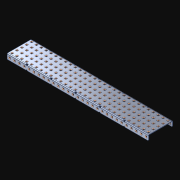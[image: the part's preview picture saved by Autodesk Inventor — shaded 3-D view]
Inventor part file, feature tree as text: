
AUTODESK INVENTOR PART (.ipt)
format: ipt  version: 2021 (Build 250183000, 183)  size: 2,302,976 bytes
history: native  units: in
note: dims shown in document units (in); Inventor stores cm internally (conversion verified against a paired STEP export)
features: extrude x204, other x204, sketch x4, pattern_linear x3
ambient origin geometry x8: Origin, YZ Plane, XZ Plane, XY Plane, X Axis, Y Axis, Z Axis, Center Point
bodies: Solid1 (feature_tree)
feature tree (415):
  pattern_linear  "Rectangular Pattern1"  Spacing1=0.182in  [1 undecoded]
  pattern_linear  "Rectangular Pattern2"  Spacing1=0.046in  [1 undecoded]
  pattern_linear  "Rectangular Pattern3"  Spacing1=0.5in  [1 undecoded]
  extrude  "Extrusion1"  Depth=0.046in
  sketch  "Sketch1"  dims[d0=0.182in]
  other  "Srf1"
  sketch  "Sketch2"  dims[d1=0.046in d2=0.0in]
  other  "Srf2"
  sketch  "Sketch3"  dims[d3=0.182in]
  other  "Srf3"
  other  "Srf4"
  other  "Srf5"
  other  "Srf6"
  other  "Srf7"
  other  "Srf8"
  other  "Srf9"
  other  "Srf10"
  other  "Srf11"
  other  "Srf12"
  other  "Srf13"
  other  "Srf14"
  other  "Srf15"
  other  "Srf16"
  other  "Srf17"
  other  "Srf18"
  other  "Srf19"
  other  "Srf20"
  other  "Srf21"
  other  "Srf22"
  other  "Srf23"
  other  "Srf24"
  other  "Srf25"
  other  "Srf26"
  other  "Srf27"
  other  "Srf28"
  other  "Srf29"
  other  "Srf30"
  other  "Srf31"
  other  "Srf38"
  other  "Srf39"
  other  "Srf40"
  other  "Srf41"
  other  "Srf42"
  other  "Srf43"
  other  "Srf44"
  other  "Srf45"
  other  "Srf46"
  other  "Srf47"
  other  "Srf48"
  other  "Srf49"
  other  "Srf50"
  other  "Srf51"
  other  "Srf52"
  other  "Srf53"
  other  "Srf54"
  other  "Srf55"
  other  "Srf56"
  other  "Srf57"
  other  "Srf58"
  other  "Srf59"
  other  "Srf60"
  other  "Srf61"
  other  "Srf62"
  other  "Srf63"
  other  "Srf64"
  other  "Srf65"
  other  "Srf72"
  other  "Srf73"
  other  "Srf74"
  other  "Srf75"
  other  "Srf76"
  other  "Srf77"
  other  "Srf78"
  other  "Srf79"
  other  "Srf80"
  other  "Srf81"
  other  "Srf82"
  other  "Srf83"
  other  "Srf84"
  other  "Srf85"
  other  "Srf86"
  other  "Srf87"
  other  "Srf88"
  other  "Srf89"
  other  "Srf90"
  other  "Srf91"
  other  "Srf92"
  other  "Srf93"
  other  "Srf94"
  other  "Srf95"
  other  "Srf96"
  other  "Srf97"
  other  "Srf98"
  other  "Srf99"
  other  "Srf100"
  other  "Srf107"
  other  "Srf108"
  other  "Srf109"
  other  "Srf110"
  other  "Srf111"
  other  "Srf112"
  other  "Srf113"
  other  "Srf114"
  other  "Srf115"
  other  "Srf116"
  other  "Srf117"
  other  "Srf118"
  other  "Srf119"
  other  "Srf120"
  other  "Srf121"
  other  "Srf122"
  other  "Srf123"
  other  "Srf124"
  other  "Srf125"
  other  "Srf126"
  other  "Srf127"
  other  "Srf128"
  other  "Srf129"
  other  "Srf130"
  other  "Srf131"
  other  "Srf132"
  other  "Srf133"
  other  "Srf134"
  other  "Srf135"
  other  "Srf142"
  other  "Srf143"
  other  "Srf144"
  other  "Srf145"
  other  "Srf146"
  other  "Srf147"
  other  "Srf148"
  other  "Srf149"
  other  "Srf150"
  other  "Srf151"
  other  "Srf152"
  other  "Srf153"
  other  "Srf154"
  other  "Srf155"
  other  "Srf156"
  other  "Srf157"
  other  "Srf158"
  other  "Srf159"
  other  "Srf160"
  other  "Srf161"
  other  "Srf162"
  other  "Srf163"
  other  "Srf164"
  other  "Srf165"
  other  "Srf166"
  other  "Srf167"
  other  "Srf168"
  other  "Srf169"
  other  "Srf170"
  other  "Srf177"
  other  "Srf178"
  other  "Srf179"
  other  "Srf180"
  other  "Srf181"
  other  "Srf182"
  other  "Srf183"
  other  "Srf184"
  other  "Srf185"
  other  "Srf186"
  other  "Srf187"
  other  "Srf188"
  other  "Srf189"
  other  "Srf190"
  other  "Srf191"
  other  "Srf192"
  other  "Srf193"
  other  "Srf194"
  other  "Srf195"
  other  "Srf196"
  other  "Srf197"
  other  "Srf198"
  other  "Srf199"
  other  "Srf200"
  other  "Srf201"
  other  "Srf202"
  other  "Srf203"
  other  "Srf204"
  other  "Srf205"
  other  "Srf212"
  other  "Srf213"
  other  "Srf214"
  other  "Srf215"
  other  "Srf216"
  other  "Srf217"
  other  "Srf218"
  other  "Srf219"
  other  "Srf220"
  other  "Srf221"
  other  "Srf222"
  other  "Srf223"
  other  "Srf224"
  other  "Srf225"
  other  "Srf226"
  other  "Srf227"
  other  "Srf228"
  other  "Srf229"
  other  "Srf230"
  other  "Srf231"
  other  "Srf232"
  other  "Srf233"
  other  "Srf234"
  other  "Srf235"
  other  "Srf236"
  other  "Srf237"
  other  "Srf238"
  other  "Srf239"
  sketch  "Sketch4"  dims[d4=0.046in d5=0.0in d6=0.182in d7=0.046in d8=0.0in d11=0.5in d12=11.4173in d14=0.5in d15=1.9685in d17=0.5in d18=11.4173in d20=0.5in d21=3.0in d22=0.0in]
  parser-record x1  (decoder bookkeeping rows leaked as tree rows — omitted from the tree; the rows remain in map.json)
  extrude  "ExtrusionSrf1"  Depth=0.046in
  extrude  "ExtrusionSrf2"  Depth=0.046in
  extrude  "ExtrusionSrf3"  Depth=0.046in
  extrude  "ExtrusionSrf4"  Depth=0.046in
  extrude  "ExtrusionSrf5"  Depth=0.046in
  extrude  "ExtrusionSrf6"  TaperAngle=0.0deg  [1 undecoded]
  extrude  "ExtrusionSrf7"  [1 undecoded]
  extrude  "ExtrusionSrf8"  [1 undecoded]
  extrude  "ExtrusionSrf9"  [1 undecoded]
  extrude  "ExtrusionSrf10"  [1 undecoded]
  extrude  "ExtrusionSrf11"  [1 undecoded]
  extrude  "ExtrusionSrf12"  [1 undecoded]
  extrude  "ExtrusionSrf13"  [1 undecoded]
  extrude  "ExtrusionSrf14"  [1 undecoded]
  extrude  "ExtrusionSrf15"  [1 undecoded]
  extrude  "ExtrusionSrf16"  [1 undecoded]
  extrude  "ExtrusionSrf17"  [1 undecoded]
  extrude  "ExtrusionSrf18"  [1 undecoded]
  extrude  "ExtrusionSrf19"  [1 undecoded]
  extrude  "ExtrusionSrf20"  [1 undecoded]
  extrude  "ExtrusionSrf21"  [1 undecoded]
  extrude  "ExtrusionSrf22"  [1 undecoded]
  extrude  "ExtrusionSrf23"  [1 undecoded]
  extrude  "ExtrusionSrf24"  [1 undecoded]
  extrude  "ExtrusionSrf25"  [1 undecoded]
  extrude  "ExtrusionSrf26"  [1 undecoded]
  extrude  "ExtrusionSrf27"  [1 undecoded]
  extrude  "ExtrusionSrf28"  [1 undecoded]
  extrude  "ExtrusionSrf29"  [1 undecoded]
  extrude  "ExtrusionSrf30"  [1 undecoded]
  extrude  "ExtrusionSrf31"  [1 undecoded]
  extrude  "ExtrusionSrf38"  [1 undecoded]
  extrude  "ExtrusionSrf39"  [1 undecoded]
  extrude  "ExtrusionSrf40"  [1 undecoded]
  extrude  "ExtrusionSrf41"  [1 undecoded]
  extrude  "ExtrusionSrf42"  [1 undecoded]
  extrude  "ExtrusionSrf43"  [1 undecoded]
  extrude  "ExtrusionSrf44"  [1 undecoded]
  extrude  "ExtrusionSrf45"  [1 undecoded]
  extrude  "ExtrusionSrf46"  [1 undecoded]
  extrude  "ExtrusionSrf47"  [1 undecoded]
  extrude  "ExtrusionSrf48"  [1 undecoded]
  extrude  "ExtrusionSrf49"  [1 undecoded]
  extrude  "ExtrusionSrf50"  [1 undecoded]
  extrude  "ExtrusionSrf51"  [1 undecoded]
  extrude  "ExtrusionSrf52"  [1 undecoded]
  extrude  "ExtrusionSrf53"  [1 undecoded]
  extrude  "ExtrusionSrf54"  [1 undecoded]
  extrude  "ExtrusionSrf55"  [1 undecoded]
  extrude  "ExtrusionSrf56"  [1 undecoded]
  extrude  "ExtrusionSrf57"  [1 undecoded]
  extrude  "ExtrusionSrf58"  [1 undecoded]
  extrude  "ExtrusionSrf59"  [1 undecoded]
  extrude  "ExtrusionSrf60"  [1 undecoded]
  extrude  "ExtrusionSrf61"  [1 undecoded]
  extrude  "ExtrusionSrf62"  [1 undecoded]
  extrude  "ExtrusionSrf63"  [1 undecoded]
  extrude  "ExtrusionSrf64"  [1 undecoded]
  extrude  "ExtrusionSrf65"  [1 undecoded]
  extrude  "ExtrusionSrf72"  [1 undecoded]
  extrude  "ExtrusionSrf73"  [1 undecoded]
  extrude  "ExtrusionSrf74"  [1 undecoded]
  extrude  "ExtrusionSrf75"  [1 undecoded]
  extrude  "ExtrusionSrf76"  [1 undecoded]
  extrude  "ExtrusionSrf77"  [1 undecoded]
  extrude  "ExtrusionSrf78"  [1 undecoded]
  extrude  "ExtrusionSrf79"  [1 undecoded]
  extrude  "ExtrusionSrf80"  [1 undecoded]
  extrude  "ExtrusionSrf81"  [1 undecoded]
  extrude  "ExtrusionSrf82"  [1 undecoded]
  extrude  "ExtrusionSrf83"  [1 undecoded]
  extrude  "ExtrusionSrf84"  [1 undecoded]
  extrude  "ExtrusionSrf85"  [1 undecoded]
  extrude  "ExtrusionSrf86"  [1 undecoded]
  extrude  "ExtrusionSrf87"  [1 undecoded]
  extrude  "ExtrusionSrf88"  [1 undecoded]
  extrude  "ExtrusionSrf89"  [1 undecoded]
  extrude  "ExtrusionSrf90"  [1 undecoded]
  extrude  "ExtrusionSrf91"  [1 undecoded]
  extrude  "ExtrusionSrf92"  [1 undecoded]
  extrude  "ExtrusionSrf93"  [1 undecoded]
  extrude  "ExtrusionSrf94"  [1 undecoded]
  extrude  "ExtrusionSrf95"  [1 undecoded]
  extrude  "ExtrusionSrf96"  [1 undecoded]
  extrude  "ExtrusionSrf97"  [1 undecoded]
  extrude  "ExtrusionSrf98"  [1 undecoded]
  extrude  "ExtrusionSrf99"  [1 undecoded]
  extrude  "ExtrusionSrf100"  [1 undecoded]
  extrude  "ExtrusionSrf107"  [1 undecoded]
  extrude  "ExtrusionSrf108"  [1 undecoded]
  extrude  "ExtrusionSrf109"  [1 undecoded]
  extrude  "ExtrusionSrf110"  [1 undecoded]
  extrude  "ExtrusionSrf111"  [1 undecoded]
  extrude  "ExtrusionSrf112"  [1 undecoded]
  extrude  "ExtrusionSrf113"  [1 undecoded]
  extrude  "ExtrusionSrf114"  [1 undecoded]
  extrude  "ExtrusionSrf115"  [1 undecoded]
  extrude  "ExtrusionSrf116"  [1 undecoded]
  extrude  "ExtrusionSrf117"  [1 undecoded]
  extrude  "ExtrusionSrf118"  [1 undecoded]
  extrude  "ExtrusionSrf119"  [1 undecoded]
  extrude  "ExtrusionSrf120"  [1 undecoded]
  extrude  "ExtrusionSrf121"  [1 undecoded]
  extrude  "ExtrusionSrf122"  [1 undecoded]
  extrude  "ExtrusionSrf123"  [1 undecoded]
  extrude  "ExtrusionSrf124"  [1 undecoded]
  extrude  "ExtrusionSrf125"  [1 undecoded]
  extrude  "ExtrusionSrf126"  [1 undecoded]
  extrude  "ExtrusionSrf127"  [1 undecoded]
  extrude  "ExtrusionSrf128"  [1 undecoded]
  extrude  "ExtrusionSrf129"  [1 undecoded]
  extrude  "ExtrusionSrf130"  [1 undecoded]
  extrude  "ExtrusionSrf131"  [1 undecoded]
  extrude  "ExtrusionSrf132"  [1 undecoded]
  extrude  "ExtrusionSrf133"  [1 undecoded]
  extrude  "ExtrusionSrf134"  [1 undecoded]
  extrude  "ExtrusionSrf135"  [1 undecoded]
  extrude  "ExtrusionSrf142"  [1 undecoded]
  extrude  "ExtrusionSrf143"  [1 undecoded]
  extrude  "ExtrusionSrf144"  [1 undecoded]
  extrude  "ExtrusionSrf145"  [1 undecoded]
  extrude  "ExtrusionSrf146"  [1 undecoded]
  extrude  "ExtrusionSrf147"  [1 undecoded]
  extrude  "ExtrusionSrf148"  [1 undecoded]
  extrude  "ExtrusionSrf149"  [1 undecoded]
  extrude  "ExtrusionSrf150"  [1 undecoded]
  extrude  "ExtrusionSrf151"  [1 undecoded]
  extrude  "ExtrusionSrf152"  [1 undecoded]
  extrude  "ExtrusionSrf153"  [1 undecoded]
  extrude  "ExtrusionSrf154"  [1 undecoded]
  extrude  "ExtrusionSrf155"  [1 undecoded]
  extrude  "ExtrusionSrf156"  [1 undecoded]
  extrude  "ExtrusionSrf157"  [1 undecoded]
  extrude  "ExtrusionSrf158"  [1 undecoded]
  extrude  "ExtrusionSrf159"  [1 undecoded]
  extrude  "ExtrusionSrf160"  [1 undecoded]
  extrude  "ExtrusionSrf161"  [1 undecoded]
  extrude  "ExtrusionSrf162"  [1 undecoded]
  extrude  "ExtrusionSrf163"  [1 undecoded]
  extrude  "ExtrusionSrf164"  [1 undecoded]
  extrude  "ExtrusionSrf165"  [1 undecoded]
  extrude  "ExtrusionSrf166"  [1 undecoded]
  extrude  "ExtrusionSrf167"  [1 undecoded]
  extrude  "ExtrusionSrf168"  [1 undecoded]
  extrude  "ExtrusionSrf169"  [1 undecoded]
  extrude  "ExtrusionSrf170"  [1 undecoded]
  extrude  "ExtrusionSrf177"  [1 undecoded]
  extrude  "ExtrusionSrf178"  [1 undecoded]
  extrude  "ExtrusionSrf179"  [1 undecoded]
  extrude  "ExtrusionSrf180"  [1 undecoded]
  extrude  "ExtrusionSrf181"  [1 undecoded]
  extrude  "ExtrusionSrf182"  [1 undecoded]
  extrude  "ExtrusionSrf183"  [1 undecoded]
  extrude  "ExtrusionSrf184"  [1 undecoded]
  extrude  "ExtrusionSrf185"  [1 undecoded]
  extrude  "ExtrusionSrf186"  [1 undecoded]
  extrude  "ExtrusionSrf187"  [1 undecoded]
  extrude  "ExtrusionSrf188"  [1 undecoded]
  extrude  "ExtrusionSrf189"  [1 undecoded]
  extrude  "ExtrusionSrf190"  [1 undecoded]
  extrude  "ExtrusionSrf191"  [1 undecoded]
  extrude  "ExtrusionSrf192"  [1 undecoded]
  extrude  "ExtrusionSrf193"  [1 undecoded]
  extrude  "ExtrusionSrf194"  [1 undecoded]
  extrude  "ExtrusionSrf195"  [1 undecoded]
  extrude  "ExtrusionSrf196"  [1 undecoded]
  extrude  "ExtrusionSrf197"  [1 undecoded]
  extrude  "ExtrusionSrf198"  [1 undecoded]
  extrude  "ExtrusionSrf199"  [1 undecoded]
  extrude  "ExtrusionSrf200"  [1 undecoded]
  extrude  "ExtrusionSrf201"  [1 undecoded]
  extrude  "ExtrusionSrf202"  [1 undecoded]
  extrude  "ExtrusionSrf203"  [1 undecoded]
  extrude  "ExtrusionSrf204"  [1 undecoded]
  extrude  "ExtrusionSrf205"  [1 undecoded]
  extrude  "ExtrusionSrf212"  [1 undecoded]
  extrude  "ExtrusionSrf213"  [1 undecoded]
  extrude  "ExtrusionSrf214"  [1 undecoded]
  extrude  "ExtrusionSrf215"  [1 undecoded]
  extrude  "ExtrusionSrf216"  [1 undecoded]
  extrude  "ExtrusionSrf217"  [1 undecoded]
  extrude  "ExtrusionSrf218"  [1 undecoded]
  extrude  "ExtrusionSrf219"  [1 undecoded]
  extrude  "ExtrusionSrf220"  [1 undecoded]
  extrude  "ExtrusionSrf221"  [1 undecoded]
  extrude  "ExtrusionSrf222"  [1 undecoded]
  extrude  "ExtrusionSrf223"  [1 undecoded]
  extrude  "ExtrusionSrf224"  [1 undecoded]
  extrude  "ExtrusionSrf225"  [1 undecoded]
  extrude  "ExtrusionSrf226"  [1 undecoded]
  extrude  "ExtrusionSrf227"  [1 undecoded]
  extrude  "ExtrusionSrf228"  [1 undecoded]
  extrude  "ExtrusionSrf229"  [1 undecoded]
  extrude  "ExtrusionSrf230"  [1 undecoded]
  extrude  "ExtrusionSrf231"  [1 undecoded]
  extrude  "ExtrusionSrf232"  [1 undecoded]
  extrude  "ExtrusionSrf233"  [1 undecoded]
  extrude  "ExtrusionSrf234"  [1 undecoded]
  extrude  "ExtrusionSrf235"  [1 undecoded]
  extrude  "ExtrusionSrf236"  [1 undecoded]
  extrude  "ExtrusionSrf237"  [1 undecoded]
  extrude  "ExtrusionSrf238"  [1 undecoded]
  extrude  "ExtrusionSrf239"  [1 undecoded]
note: 201 required parameter values undecoded (feature->parameter linkage not recoverable at this tier; creation-order binding heuristic only, values carry confidence <= 0.55)
